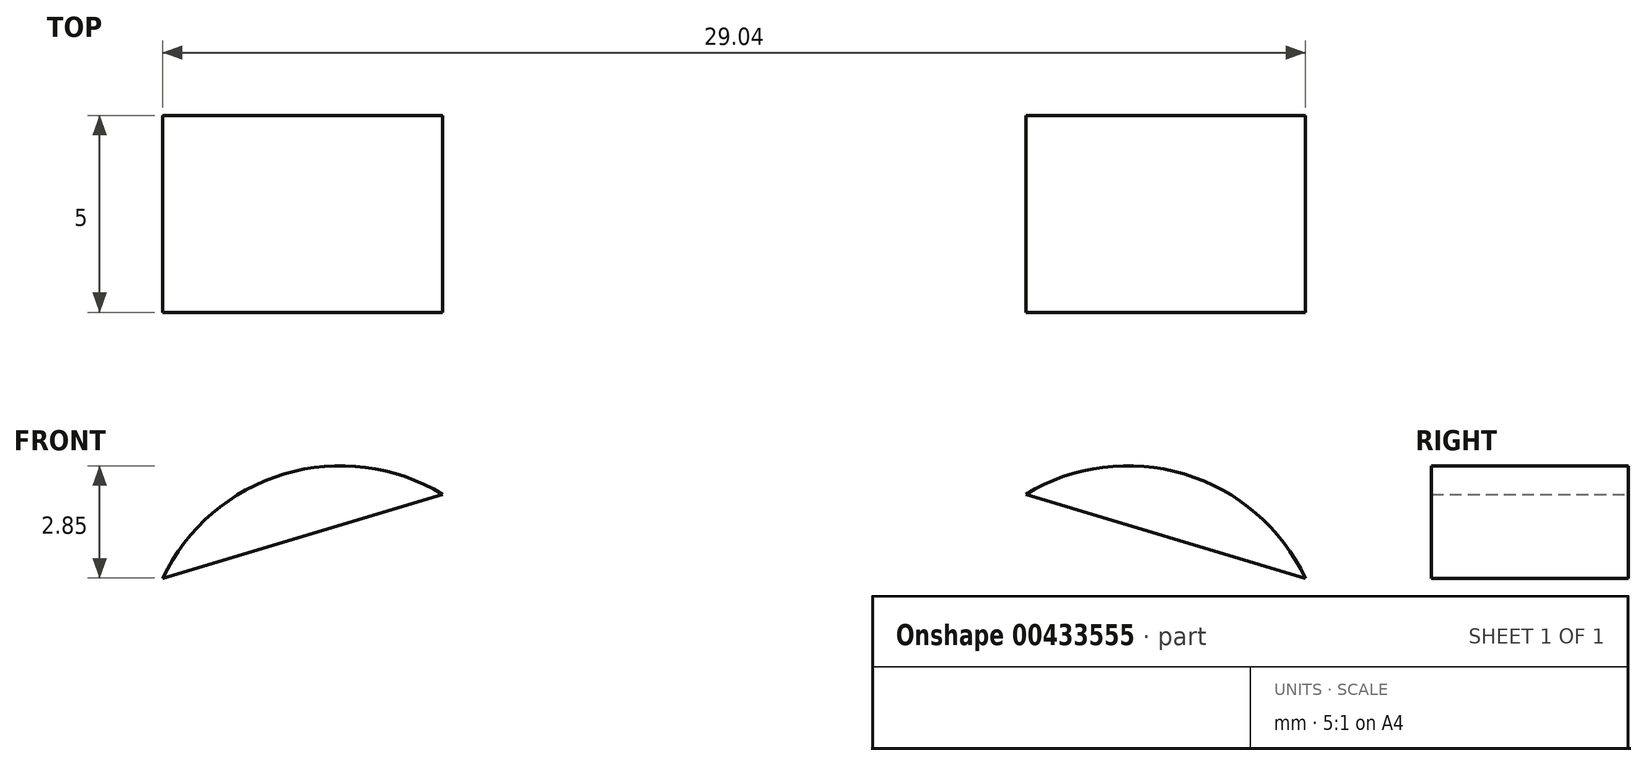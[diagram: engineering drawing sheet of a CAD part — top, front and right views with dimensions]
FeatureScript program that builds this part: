
annotation { "Feature Type Name" : "Feature", "Feature Type Description" : "" }
export const myFeature = defineFeature(function(context is Context, id is Id, definition is map)
    precondition{}
    {
        {
            assignVariable(context, id + "F0", {"name" : "eyeDiameter", "anyValue" : 10});
        }
        {
            var Q0;
            Q0=qCreatedBy(makeId("Front.planeOp"),FACE);
            var sketch = newSketch(context, id + "F1", { "sketchPlane" : qUnion([Q0])});
            skCircle(sketch, "E0", {"center": v(0, 0) * mm, "radius": 5 * mm});
            skLineSegment(sketch, "E1", {"start": v(5, 0) * mm, "end": v(5, -5) * mm, "construction": true});
            skLineSegment(sketch, "E2", {"start": v(5, 0) * mm, "end": v(5, 5) * mm, "construction": true});
            skLineSegment(sketch, "E3", {"start": v(-5, 0) * mm, "end": v(-5, -5) * mm, "construction": true});
            skLineSegment(sketch, "E4", {"start": v(-5, 0) * mm, "end": v(-5, 2) * mm, "construction": true});
            skLineSegment(sketch, "E5", {"start": v(-5, 2) * mm, "end": v(5, 5) * mm});
            skLineSegment(sketch, "E6", {"start": v(-5, -5) * mm, "end": v(5, -5) * mm});
            skSolve(sketch);
        }
        {
            var Q0;
            {var subQ0=sQuery(id+"F1.wireOp",EDGE,"E5");var subQ1=sQuery(id+"F1.wireOp",EDGE,"E0");var subQ2=makeQuery(id+"F1.imprint","INTERSECT",VERTEX,{"disambiguationData":[OD(0.0)],"derivedFrom":[subQ1,subQ0]});Q0=makeQuery(id+"F1.imprint","IMPRINT",FACE,{"disambiguationData":[TD([[makeQuery(id+"F1.imprint","IMPRINT",EDGE,{"disambiguationData":[TD([[subQ2,-1.0]])],"derivedFrom":subQ1}),1.0]])]});}
            extrude(context, id + "F2", {"entities" : qUnion([Q0]), "depth" : 5 * mm});
        }
        {
            var Q0;
            Q0=qCreatedBy(makeId("Right.planeOp"),FACE);
            cPlane(context, id + "F3", {"entities" : qUnion([Q0]), "cplaneType" : CPlaneType.OFFSET, "offset" : (getVariable(context, 'eyeDiameter')) * mm, "width" : 150 * mm, "height" : 150 * mm});
        }
        {
            var Q0;
            Q0=makeQuery(id+"F2.opExtrude","SWEPT_BODY",BODY,{"disambiguationData":[OSD([sQuery(id+"F1.wireOp",EDGE,"E0")])]});
            var Q1;
            Q1=qCreatedBy(id+"F3.planeOp",FACE);
            mirror(context, id + "F4", {"entities" : qUnion([Q0]), "mirrorPlane" : qUnion([Q1])});
        }
    });
